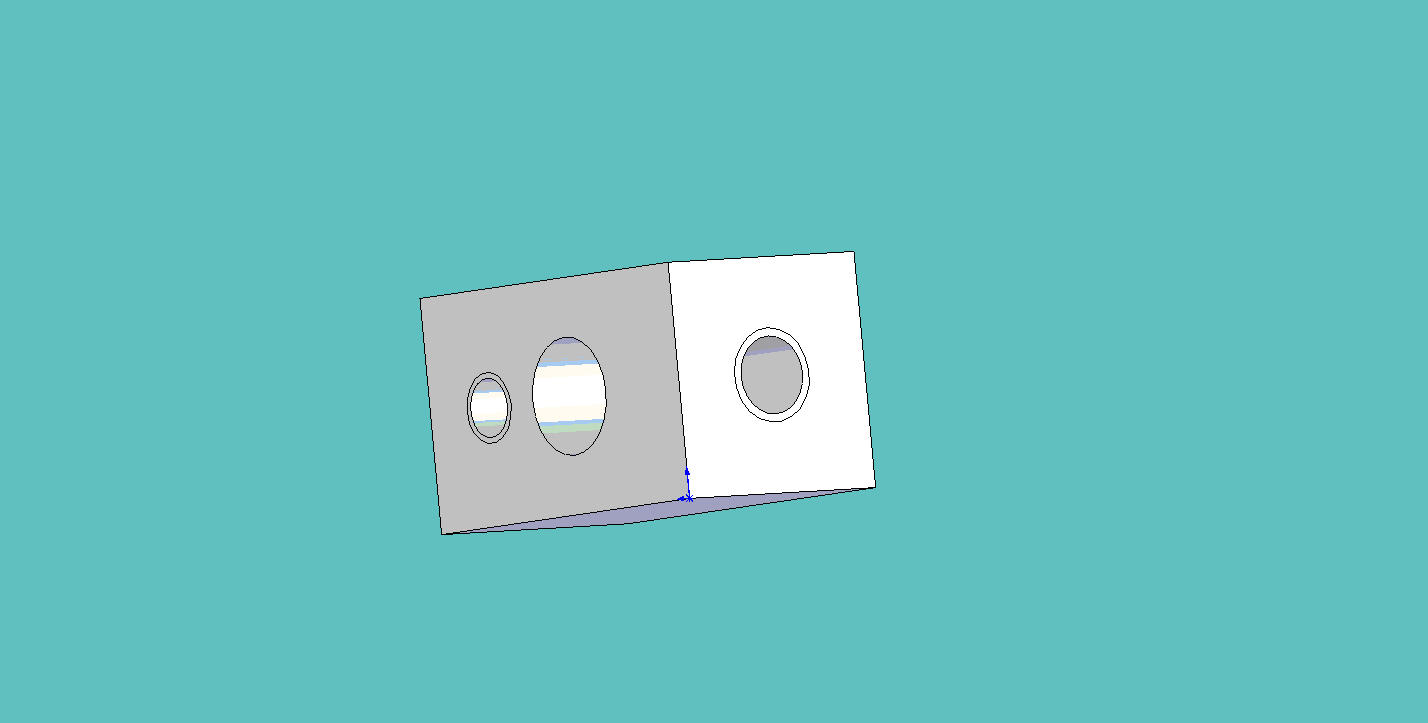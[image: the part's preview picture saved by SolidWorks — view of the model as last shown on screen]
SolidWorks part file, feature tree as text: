
SOLIDWORKS PART (.sldprt)
format: sldprt  version: not decoded by parser v0  size: 145,920 bytes
history: native  units: mm
features: sketch x6, plane x3, hole x2, thread x2, material x1, extrude x1, cut_extrude x1 (+10 scaffold rows collapsed)
feature tree (26):
  scaffold x10  (default folders/planes/origin — collapsed)
  material  "Matériau <non spécifié>"
  plane  "Plan de face"
  plane  "Plan de dessus"
  plane  "Plan de droite"
  sketch  "Esquisse1"  dims[D1=10.0mm D2=10.0mm]
  extrude  "Extrusion1"  Depth=17mm
  sketch  "Esquisse2"  dims[D2=5.0mm D1=7.5mm]
  cut_extrude  "Enlèv. mat.-Extru.1"  [1 undecoded]
  hole  "Trou taraudé M3x0.51"  Diameter=2.5mm Depth=10mm
  sketch  "Esquisse3D1"  dims[D1=5.5mm]
  sketch  "Esquisse3"  dims[hole-wizard template sketch: 60 standard entries collapsed; hole parameters kept: c18.Profondeur du trou pour taraudage jusqu'au prochain=10.0mm]
  thread  "Filetage de perçage1"  Diameter=3mm  [1 undecoded]
  hole  "Trou taraudé M4x0.71"  [1 undecoded]
  sketch  "Esquisse3D2"  dims[c1.D1=~5.505316mm c1.D3=5.0mm c1.D2=~3.858728mm c2.D1=5.0mm c2.D2=5.0mm]
  thread  "Filetage de perçage2"  Diameter=5.621836mm  [1 undecoded]
  sketch  "Esquisse4"  dims[hole-wizard template sketch: 47 standard entries collapsed; hole parameters kept: c15.Profondeur du trou pour taraudage=8.0mm c15.D3=~14.816244mm c15.Angle de pointe=118.0deg]
decode coverage: 10 of 12 modeling features carry decoded parameters
note: ~ marks probable driven/reference dimensions
note: 4 parameter values undecoded
note: suppression state not decoded; provenance and decode notes live in map.json
